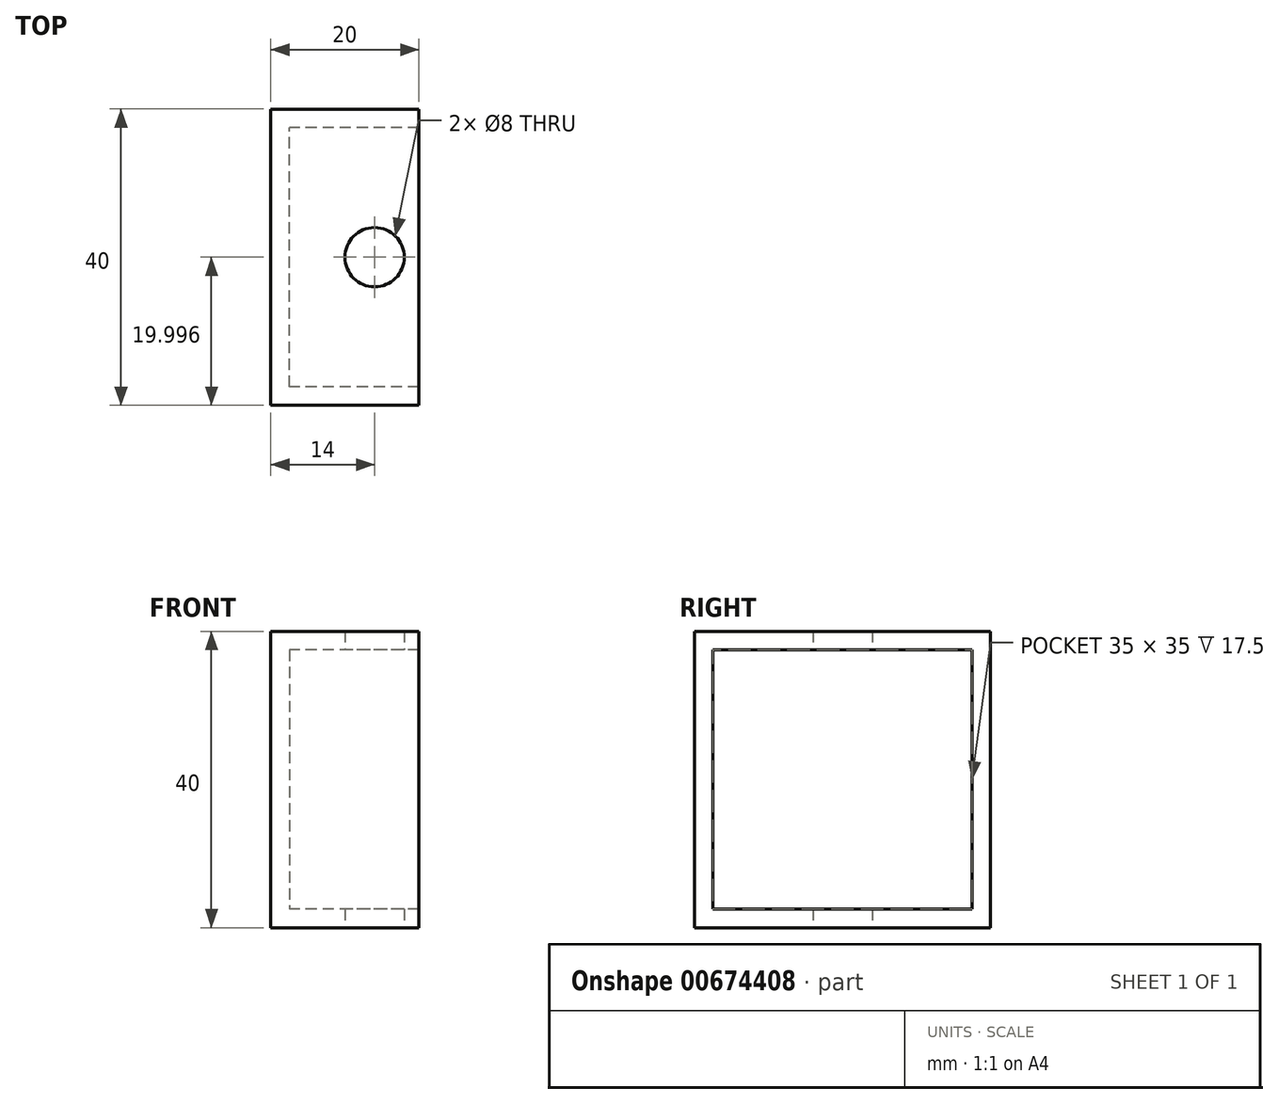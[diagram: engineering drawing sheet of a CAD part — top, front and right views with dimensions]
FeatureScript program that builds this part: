
annotation { "Feature Type Name" : "Feature", "Feature Type Description" : "" }
export const myFeature = defineFeature(function(context is Context, id is Id, definition is map)
    precondition{}
    {
        {
            var Q0;
            Q0=qCreatedBy(makeId("Right.planeOp"),FACE);
            var sketch = newSketch(context, id + "F0", { "sketchPlane" : qUnion([Q0])});
            skLineSegment(sketch, "E0.bottom", {"start": v(-16.82, 24.1) * mm, "end": v(23.18, 24.1) * mm});
            skLineSegment(sketch, "E0.top", {"start": v(-16.82, -15.9) * mm, "end": v(23.18, -15.9) * mm});
            skLineSegment(sketch, "E0.left", {"start": v(-16.82, 24.1) * mm, "end": v(-16.82, -15.9) * mm});
            skLineSegment(sketch, "E0.right", {"start": v(23.18, 24.1) * mm, "end": v(23.18, -15.9) * mm});
            skSolve(sketch);
        }
        {
            var Q0;
            Q0=makeQuery(id+"F0.imprint","IMPRINT",FACE,{"disambiguationData":[TD([[makeQuery(id+"F0.imprint","IMPRINT",EDGE,{"derivedFrom":sQuery(id+"F0.wireOp",EDGE,"E0.bottom")}),-1.0]])]});
            extrude(context, id + "F1", {"entities" : qUnion([Q0]), "depth" : 20 * mm, "offsetDistance" : 25 * mm});
        }
        {
            var Q0;
            Q0=makeQuery(id+"F1.opExtrude","CAP_FACE",FACE,{"disambiguationData":[OSD([sQuery(id+"F0.wireOp",EDGE,"E0.bottom"),sQuery(id+"F0.wireOp",EDGE,"E0.top"),sQuery(id+"F0.wireOp",EDGE,"E0.left"),sQuery(id+"F0.wireOp",EDGE,"E0.right")])],"isStart":false});
            shell(context, id + "F2", {"entities" : qUnion([Q0]), "thickness" : 2.5 * mm});
        }
        {
            var Q0;
            Q0=makeQuery(id+"F1.opExtrude","SWEPT_FACE",FACE,{"disambiguationData":[OSD([sQuery(id+"F0.wireOp",EDGE,"E0.top")])]});
            var sketch = newSketch(context, id + "F3", { "sketchPlane" : qUnion([Q0])});
            skCircle(sketch, "E1", {"center": v(14, -3.18) * mm, "radius": 4 * mm});
            skSolve(sketch);
        }
        {
            var Q0;
            Q0=makeQuery(id+"F3.imprint","IMPRINT",FACE,{"disambiguationData":[TD([[makeQuery(id+"F3.imprint","IMPRINT",EDGE,{"derivedFrom":sQuery(id+"F3.wireOp",EDGE,"E1")}),1.0]])]});
            extrude(context, id + "F4", {"entities" : qUnion([Q0]), "operationType" : NewBodyOperationType.REMOVE, "endBound" : BoundingType.THROUGH_ALL, "oppositeDirection" : true, "depth" : 25 * mm, "offsetDistance" : 25 * mm});
        }
    });
